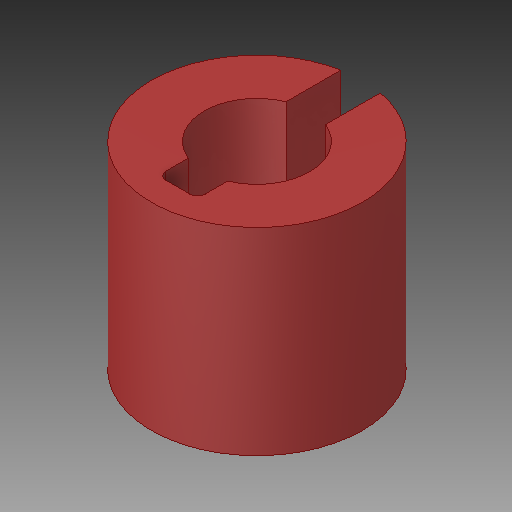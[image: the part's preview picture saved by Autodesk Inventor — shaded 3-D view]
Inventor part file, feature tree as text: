
AUTODESK INVENTOR PART (.ipt)
format: ipt  version: 2017 (Build 210142000, 142)  size: 102,912 bytes
history: native  units: in
note: dims shown in document units (in); Inventor stores cm internally (conversion verified against a paired STEP export)
features: fillet x1
ambient origin geometry x8: Origin, YZ Plane, XZ Plane, XY Plane, X Axis, Y Axis, Z Axis, Center Point
bodies: Solid1 (feature_tree)
feature tree (1):
  fillet  "Fillet1"  [1 undecoded]
note: 1 required parameter value undecoded (feature->parameter linkage not recoverable at this tier; creation-order binding heuristic only, values carry confidence <= 0.55)
